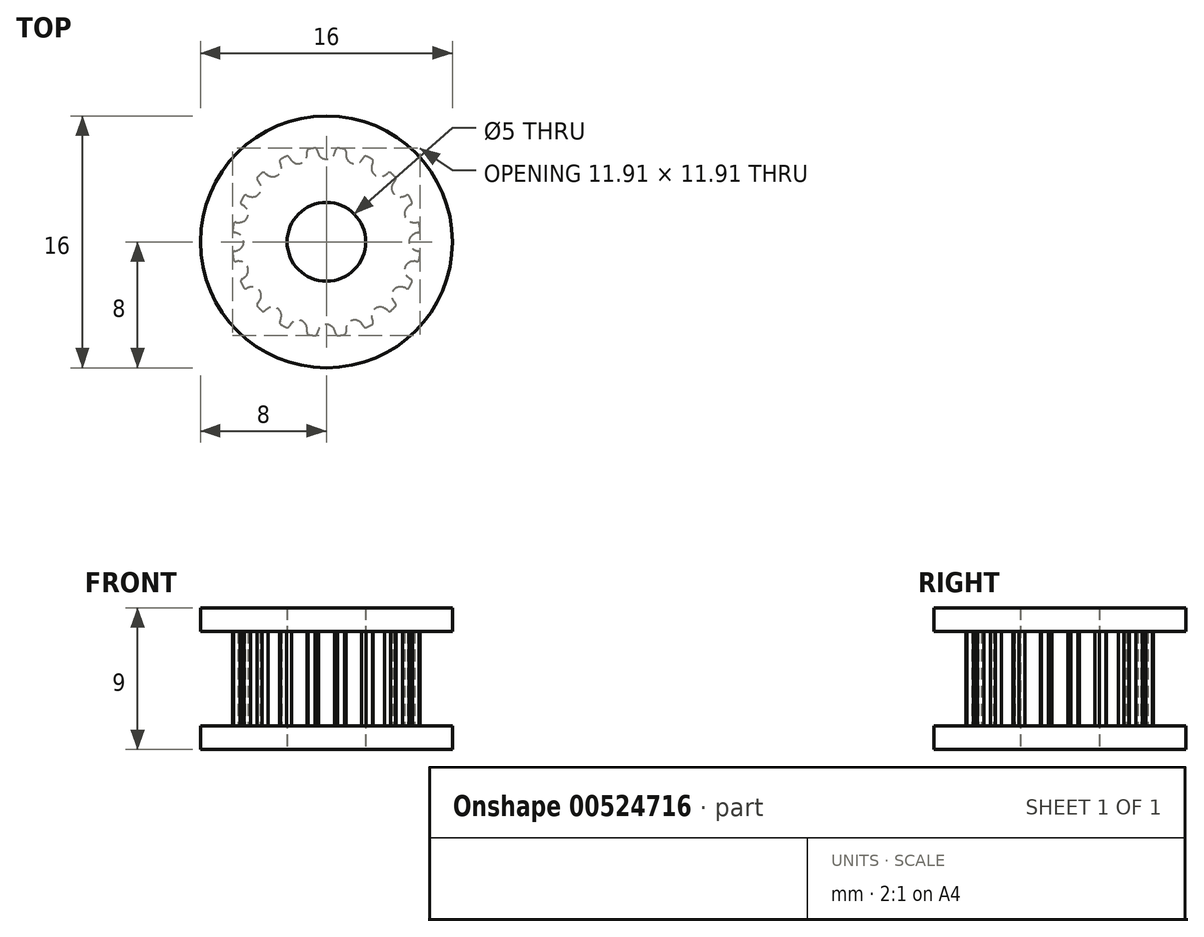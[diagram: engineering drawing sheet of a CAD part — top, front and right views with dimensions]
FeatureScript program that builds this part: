
annotation { "Feature Type Name" : "Feature", "Feature Type Description" : "" }
export const myFeature = defineFeature(function(context is Context, id is Id, definition is map)
    precondition{}
    {
        {
            var Q0;
            Q0=qCreatedBy(makeId("Top.planeOp"),FACE);
            var sketch = newSketch(context, id + "F0", { "sketchPlane" : qUnion([Q0])});
            skLineSegment(sketch, "E0", {"start": v(-19.17, 17.78) * mm, "end": v(-18.17, 17.78) * mm});
            skLineSegment(sketch, "E1", {"start": v(-18.17, 17.78) * mm, "end": v(-18.17, 18.4) * mm});
            skArc(sketch, "E2", {"start": v(-18.67, 18.85) * mm, "mid": v(-18.88, 19.07) * mm, "end": v(-19.17, 19.16) * mm});
            skArc(sketch, "E3", {"start": v(-18.58, 18.54) * mm, "mid": v(-18.61, 18.7) * mm, "end": v(-18.67, 18.85) * mm});
            skArc(sketch, "E4", {"start": v(-18.58, 18.54) * mm, "mid": v(-18.53, 18.44) * mm, "end": v(-18.43, 18.4) * mm});
            skLineSegment(sketch, "E5", {"start": v(-18.43, 18.4) * mm, "end": v(-18.17, 18.4) * mm});
            skArc(sketch, "E6.0.MirrorCS", {"start": v(-19.67, 18.85) * mm, "mid": v(-19.47, 19.07) * mm, "end": v(-19.17, 19.16) * mm});
            skArc(sketch, "E7.0.MirrorCS", {"start": v(-19.76, 18.54) * mm, "mid": v(-19.73, 18.7) * mm, "end": v(-19.67, 18.85) * mm});
            skArc(sketch, "E8.0.MirrorCS", {"start": v(-19.76, 18.54) * mm, "mid": v(-19.81, 18.44) * mm, "end": v(-19.91, 18.4) * mm});
            skLineSegment(sketch, "E9.0.MirrorCS", {"start": v(-19.91, 18.4) * mm, "end": v(-20.17, 18.4) * mm});
            skLineSegment(sketch, "E10.0.MirrorCS", {"start": v(-20.17, 17.78) * mm, "end": v(-20.17, 18.4) * mm});
            skLineSegment(sketch, "E11.0.MirrorCS", {"start": v(-19.17, 17.78) * mm, "end": v(-20.17, 17.78) * mm});
            skLineSegment(sketch, "E12.direction1", {"start": v(-20.17, 17.78) * mm, "end": v(-18.17, 17.78) * mm, "construction": true});
            skLineSegment(sketch, "E13", {"start": v(-20.17, 18.15) * mm, "end": v(-18.17, 18.15) * mm, "construction": true});
            skPoint(sketch, "E14", {"position": v(0, -5.25) * mm});
            skArc(sketch, "E15", {"start": v(0.51, -5.6) * mm, "mid": v(0, -5.25) * mm, "end": v(-0.51, -5.6) * mm});
            skArc(sketch, "E16", {"start": v(-0.51, -5.6) * mm, "mid": v(-0.56, -5.71) * mm, "end": v(-0.59, -5.83) * mm});
            skArc(sketch, "E17", {"start": v(0.59, -5.83) * mm, "mid": v(0.56, -5.71) * mm, "end": v(0.51, -5.6) * mm});
            skArc(sketch, "E18", {"start": v(0.72, -5.96) * mm, "mid": v(0.94, -5.93) * mm, "end": v(1.16, -5.89) * mm});
            skArc(sketch, "E19", {"start": v(0.59, -5.83) * mm, "mid": v(0.66, -5.94) * mm, "end": v(0.8, -5.95) * mm});
            skArc(sketch, "E20", {"start": v(-0.59, -5.83) * mm, "mid": v(-0.66, -5.94) * mm, "end": v(-0.8, -5.95) * mm});
            skArc(sketch, "E21.1.0", {"start": v(2.22, -5.16) * mm, "mid": v(1.62, -5) * mm, "end": v(1.24, -5.48) * mm});
            skPoint(sketch, "E21.1.1", {"position": v(1.62, -5) * mm});
            skArc(sketch, "E21.1.2", {"start": v(1.24, -5.48) * mm, "mid": v(1.23, -5.6) * mm, "end": v(1.24, -5.73) * mm});
            skArc(sketch, "E21.1.3", {"start": v(2.36, -5.37) * mm, "mid": v(2.47, -5.44) * mm, "end": v(2.6, -5.41) * mm});
            skArc(sketch, "E21.1.4", {"start": v(1.24, -5.73) * mm, "mid": v(1.2, -5.85) * mm, "end": v(1.08, -5.9) * mm});
            skArc(sketch, "E21.1.5", {"start": v(2.36, -5.37) * mm, "mid": v(2.3, -5.26) * mm, "end": v(2.22, -5.16) * mm});
            skArc(sketch, "E22.3.2.0", {"start": v(3.7, -4.22) * mm, "mid": v(3.09, -4.25) * mm, "end": v(2.87, -4.83) * mm});
            skPoint(sketch, "E22.4.2.0", {"position": v(3.09, -4.25) * mm});
            skArc(sketch, "E22.5.2.0", {"start": v(2.87, -4.83) * mm, "mid": v(2.9, -4.95) * mm, "end": v(2.95, -5.07) * mm});
            skArc(sketch, "E22.9.2.0", {"start": v(3.9, -4.37) * mm, "mid": v(4.03, -4.41) * mm, "end": v(4.14, -4.35) * mm});
            skArc(sketch, "E22.13.2.0", {"start": v(2.95, -5.07) * mm, "mid": v(2.95, -5.2) * mm, "end": v(2.85, -5.28) * mm});
            skArc(sketch, "E22.17.2.0", {"start": v(3.9, -4.37) * mm, "mid": v(3.81, -4.3) * mm, "end": v(3.7, -4.22) * mm});
            skArc(sketch, "E22.3.3.0", {"start": v(4.83, -2.87) * mm, "mid": v(4.25, -3.09) * mm, "end": v(4.22, -3.7) * mm});
            skPoint(sketch, "E22.4.3.0", {"position": v(4.25, -3.09) * mm});
            skArc(sketch, "E22.5.3.0", {"start": v(4.22, -3.7) * mm, "mid": v(4.3, -3.81) * mm, "end": v(4.37, -3.9) * mm});
            skArc(sketch, "E22.9.3.0", {"start": v(5.07, -2.95) * mm, "mid": v(5.2, -2.95) * mm, "end": v(5.28, -2.85) * mm});
            skArc(sketch, "E22.13.3.0", {"start": v(4.37, -3.9) * mm, "mid": v(4.41, -4.03) * mm, "end": v(4.35, -4.14) * mm});
            skArc(sketch, "E22.17.3.0", {"start": v(5.07, -2.95) * mm, "mid": v(4.95, -2.9) * mm, "end": v(4.83, -2.87) * mm});
            skArc(sketch, "E22.3.4.0", {"start": v(5.48, -1.24) * mm, "mid": v(5, -1.62) * mm, "end": v(5.16, -2.22) * mm});
            skPoint(sketch, "E22.4.4.0", {"position": v(5, -1.62) * mm});
            skArc(sketch, "E22.5.4.0", {"start": v(5.16, -2.22) * mm, "mid": v(5.26, -2.3) * mm, "end": v(5.37, -2.36) * mm});
            skArc(sketch, "E22.9.4.0", {"start": v(5.73, -1.24) * mm, "mid": v(5.85, -1.2) * mm, "end": v(5.9, -1.08) * mm});
            skArc(sketch, "E22.13.4.0", {"start": v(5.37, -2.36) * mm, "mid": v(5.44, -2.47) * mm, "end": v(5.41, -2.6) * mm});
            skArc(sketch, "E22.17.4.0", {"start": v(5.73, -1.24) * mm, "mid": v(5.6, -1.23) * mm, "end": v(5.48, -1.24) * mm});
            skArc(sketch, "E22.3.5.0", {"start": v(5.6, 0.51) * mm, "mid": v(5.25, 0) * mm, "end": v(5.6, -0.51) * mm});
            skPoint(sketch, "E22.4.5.0", {"position": v(5.25, 0) * mm});
            skArc(sketch, "E22.5.5.0", {"start": v(5.6, -0.51) * mm, "mid": v(5.71, -0.56) * mm, "end": v(5.83, -0.59) * mm});
            skArc(sketch, "E22.9.5.0", {"start": v(5.83, 0.59) * mm, "mid": v(5.94, 0.66) * mm, "end": v(5.95, 0.8) * mm});
            skArc(sketch, "E22.13.5.0", {"start": v(5.83, -0.59) * mm, "mid": v(5.94, -0.66) * mm, "end": v(5.95, -0.8) * mm});
            skArc(sketch, "E22.17.5.0", {"start": v(5.83, 0.59) * mm, "mid": v(5.71, 0.56) * mm, "end": v(5.6, 0.51) * mm});
            skArc(sketch, "E22.3.6.0", {"start": v(5.16, 2.22) * mm, "mid": v(5, 1.62) * mm, "end": v(5.48, 1.24) * mm});
            skPoint(sketch, "E22.4.6.0", {"position": v(5, 1.62) * mm});
            skArc(sketch, "E22.5.6.0", {"start": v(5.48, 1.24) * mm, "mid": v(5.6, 1.23) * mm, "end": v(5.73, 1.24) * mm});
            skArc(sketch, "E22.9.6.0", {"start": v(5.37, 2.36) * mm, "mid": v(5.44, 2.47) * mm, "end": v(5.41, 2.6) * mm});
            skArc(sketch, "E22.13.6.0", {"start": v(5.73, 1.24) * mm, "mid": v(5.85, 1.2) * mm, "end": v(5.9, 1.08) * mm});
            skArc(sketch, "E22.17.6.0", {"start": v(5.37, 2.36) * mm, "mid": v(5.26, 2.3) * mm, "end": v(5.16, 2.22) * mm});
            skArc(sketch, "E22.3.7.0", {"start": v(4.22, 3.7) * mm, "mid": v(4.25, 3.09) * mm, "end": v(4.83, 2.87) * mm});
            skPoint(sketch, "E22.4.7.0", {"position": v(4.25, 3.09) * mm});
            skArc(sketch, "E22.5.7.0", {"start": v(4.83, 2.87) * mm, "mid": v(4.95, 2.9) * mm, "end": v(5.07, 2.95) * mm});
            skArc(sketch, "E22.9.7.0", {"start": v(4.37, 3.9) * mm, "mid": v(4.41, 4.03) * mm, "end": v(4.35, 4.14) * mm});
            skArc(sketch, "E22.13.7.0", {"start": v(5.07, 2.95) * mm, "mid": v(5.2, 2.95) * mm, "end": v(5.28, 2.85) * mm});
            skArc(sketch, "E22.17.7.0", {"start": v(4.37, 3.9) * mm, "mid": v(4.3, 3.81) * mm, "end": v(4.22, 3.7) * mm});
            skArc(sketch, "E22.3.8.0", {"start": v(2.87, 4.83) * mm, "mid": v(3.09, 4.25) * mm, "end": v(3.7, 4.22) * mm});
            skPoint(sketch, "E22.4.8.0", {"position": v(3.09, 4.25) * mm});
            skArc(sketch, "E22.5.8.0", {"start": v(3.7, 4.22) * mm, "mid": v(3.81, 4.3) * mm, "end": v(3.9, 4.37) * mm});
            skArc(sketch, "E22.9.8.0", {"start": v(2.95, 5.07) * mm, "mid": v(2.95, 5.2) * mm, "end": v(2.85, 5.28) * mm});
            skArc(sketch, "E22.13.8.0", {"start": v(3.9, 4.37) * mm, "mid": v(4.03, 4.41) * mm, "end": v(4.14, 4.35) * mm});
            skArc(sketch, "E22.17.8.0", {"start": v(2.95, 5.07) * mm, "mid": v(2.9, 4.95) * mm, "end": v(2.87, 4.83) * mm});
            skArc(sketch, "E22.3.9.0", {"start": v(1.24, 5.48) * mm, "mid": v(1.62, 5) * mm, "end": v(2.22, 5.16) * mm});
            skPoint(sketch, "E22.4.9.0", {"position": v(1.62, 5) * mm});
            skArc(sketch, "E22.5.9.0", {"start": v(2.22, 5.16) * mm, "mid": v(2.3, 5.26) * mm, "end": v(2.36, 5.37) * mm});
            skArc(sketch, "E22.9.9.0", {"start": v(1.24, 5.73) * mm, "mid": v(1.2, 5.85) * mm, "end": v(1.08, 5.9) * mm});
            skArc(sketch, "E22.13.9.0", {"start": v(2.36, 5.37) * mm, "mid": v(2.47, 5.44) * mm, "end": v(2.6, 5.41) * mm});
            skArc(sketch, "E22.17.9.0", {"start": v(1.24, 5.73) * mm, "mid": v(1.23, 5.6) * mm, "end": v(1.24, 5.48) * mm});
            skArc(sketch, "E22.3.10.0", {"start": v(-0.51, 5.6) * mm, "mid": v(0, 5.25) * mm, "end": v(0.51, 5.6) * mm});
            skPoint(sketch, "E22.4.10.0", {"position": v(0, 5.25) * mm});
            skArc(sketch, "E22.5.10.0", {"start": v(0.51, 5.6) * mm, "mid": v(0.56, 5.71) * mm, "end": v(0.59, 5.83) * mm});
            skArc(sketch, "E22.9.10.0", {"start": v(-0.59, 5.83) * mm, "mid": v(-0.66, 5.94) * mm, "end": v(-0.8, 5.95) * mm});
            skArc(sketch, "E22.13.10.0", {"start": v(0.59, 5.83) * mm, "mid": v(0.66, 5.94) * mm, "end": v(0.8, 5.95) * mm});
            skArc(sketch, "E22.17.10.0", {"start": v(-0.59, 5.83) * mm, "mid": v(-0.56, 5.71) * mm, "end": v(-0.51, 5.6) * mm});
            skArc(sketch, "E22.3.11.0", {"start": v(-2.22, 5.16) * mm, "mid": v(-1.62, 5) * mm, "end": v(-1.24, 5.48) * mm});
            skPoint(sketch, "E22.4.11.0", {"position": v(-1.62, 5) * mm});
            skArc(sketch, "E22.5.11.0", {"start": v(-1.24, 5.48) * mm, "mid": v(-1.23, 5.6) * mm, "end": v(-1.24, 5.73) * mm});
            skArc(sketch, "E22.9.11.0", {"start": v(-2.36, 5.37) * mm, "mid": v(-2.47, 5.44) * mm, "end": v(-2.6, 5.41) * mm});
            skArc(sketch, "E22.13.11.0", {"start": v(-1.24, 5.73) * mm, "mid": v(-1.2, 5.85) * mm, "end": v(-1.08, 5.9) * mm});
            skArc(sketch, "E22.17.11.0", {"start": v(-2.36, 5.37) * mm, "mid": v(-2.3, 5.26) * mm, "end": v(-2.22, 5.16) * mm});
            skArc(sketch, "E22.3.12.0", {"start": v(-3.7, 4.22) * mm, "mid": v(-3.09, 4.25) * mm, "end": v(-2.87, 4.83) * mm});
            skPoint(sketch, "E22.4.12.0", {"position": v(-3.09, 4.25) * mm});
            skArc(sketch, "E22.5.12.0", {"start": v(-2.87, 4.83) * mm, "mid": v(-2.9, 4.95) * mm, "end": v(-2.95, 5.07) * mm});
            skArc(sketch, "E22.9.12.0", {"start": v(-3.9, 4.37) * mm, "mid": v(-4.03, 4.41) * mm, "end": v(-4.14, 4.35) * mm});
            skArc(sketch, "E22.13.12.0", {"start": v(-2.95, 5.07) * mm, "mid": v(-2.95, 5.2) * mm, "end": v(-2.85, 5.28) * mm});
            skArc(sketch, "E22.17.12.0", {"start": v(-3.9, 4.37) * mm, "mid": v(-3.81, 4.3) * mm, "end": v(-3.7, 4.22) * mm});
            skArc(sketch, "E22.3.13.0", {"start": v(-4.83, 2.87) * mm, "mid": v(-4.25, 3.09) * mm, "end": v(-4.22, 3.7) * mm});
            skPoint(sketch, "E22.4.13.0", {"position": v(-4.25, 3.09) * mm});
            skArc(sketch, "E22.5.13.0", {"start": v(-4.22, 3.7) * mm, "mid": v(-4.3, 3.81) * mm, "end": v(-4.37, 3.9) * mm});
            skArc(sketch, "E22.9.13.0", {"start": v(-5.07, 2.95) * mm, "mid": v(-5.2, 2.95) * mm, "end": v(-5.28, 2.85) * mm});
            skArc(sketch, "E22.13.13.0", {"start": v(-4.37, 3.9) * mm, "mid": v(-4.41, 4.03) * mm, "end": v(-4.35, 4.14) * mm});
            skArc(sketch, "E22.17.13.0", {"start": v(-5.07, 2.95) * mm, "mid": v(-4.95, 2.9) * mm, "end": v(-4.83, 2.87) * mm});
            skArc(sketch, "E22.3.14.0", {"start": v(-5.48, 1.24) * mm, "mid": v(-5, 1.62) * mm, "end": v(-5.16, 2.22) * mm});
            skPoint(sketch, "E22.4.14.0", {"position": v(-5, 1.62) * mm});
            skArc(sketch, "E22.5.14.0", {"start": v(-5.16, 2.22) * mm, "mid": v(-5.26, 2.3) * mm, "end": v(-5.37, 2.36) * mm});
            skArc(sketch, "E22.9.14.0", {"start": v(-5.73, 1.24) * mm, "mid": v(-5.85, 1.2) * mm, "end": v(-5.9, 1.08) * mm});
            skArc(sketch, "E22.13.14.0", {"start": v(-5.37, 2.36) * mm, "mid": v(-5.44, 2.47) * mm, "end": v(-5.41, 2.6) * mm});
            skArc(sketch, "E22.17.14.0", {"start": v(-5.73, 1.24) * mm, "mid": v(-5.6, 1.23) * mm, "end": v(-5.48, 1.24) * mm});
            skArc(sketch, "E22.3.15.0", {"start": v(-5.6, -0.51) * mm, "mid": v(-5.25, 0) * mm, "end": v(-5.6, 0.51) * mm});
            skPoint(sketch, "E22.4.15.0", {"position": v(-5.25, 0) * mm});
            skArc(sketch, "E22.5.15.0", {"start": v(-5.6, 0.51) * mm, "mid": v(-5.71, 0.56) * mm, "end": v(-5.83, 0.59) * mm});
            skArc(sketch, "E22.9.15.0", {"start": v(-5.83, -0.59) * mm, "mid": v(-5.94, -0.66) * mm, "end": v(-5.95, -0.8) * mm});
            skArc(sketch, "E22.13.15.0", {"start": v(-5.83, 0.59) * mm, "mid": v(-5.94, 0.66) * mm, "end": v(-5.95, 0.8) * mm});
            skArc(sketch, "E22.17.15.0", {"start": v(-5.83, -0.59) * mm, "mid": v(-5.71, -0.56) * mm, "end": v(-5.6, -0.51) * mm});
            skArc(sketch, "E22.3.16.0", {"start": v(-5.16, -2.22) * mm, "mid": v(-5, -1.62) * mm, "end": v(-5.48, -1.24) * mm});
            skPoint(sketch, "E22.4.16.0", {"position": v(-5, -1.62) * mm});
            skArc(sketch, "E22.5.16.0", {"start": v(-5.48, -1.24) * mm, "mid": v(-5.6, -1.23) * mm, "end": v(-5.73, -1.24) * mm});
            skArc(sketch, "E22.9.16.0", {"start": v(-5.37, -2.36) * mm, "mid": v(-5.44, -2.47) * mm, "end": v(-5.41, -2.6) * mm});
            skArc(sketch, "E22.13.16.0", {"start": v(-5.73, -1.24) * mm, "mid": v(-5.85, -1.2) * mm, "end": v(-5.9, -1.08) * mm});
            skArc(sketch, "E22.17.16.0", {"start": v(-5.37, -2.36) * mm, "mid": v(-5.26, -2.3) * mm, "end": v(-5.16, -2.22) * mm});
            skArc(sketch, "E22.3.17.0", {"start": v(-4.22, -3.7) * mm, "mid": v(-4.25, -3.09) * mm, "end": v(-4.83, -2.87) * mm});
            skPoint(sketch, "E22.4.17.0", {"position": v(-4.25, -3.09) * mm});
            skArc(sketch, "E22.5.17.0", {"start": v(-4.83, -2.87) * mm, "mid": v(-4.95, -2.9) * mm, "end": v(-5.07, -2.95) * mm});
            skArc(sketch, "E22.9.17.0", {"start": v(-4.37, -3.9) * mm, "mid": v(-4.41, -4.03) * mm, "end": v(-4.35, -4.14) * mm});
            skArc(sketch, "E22.13.17.0", {"start": v(-5.07, -2.95) * mm, "mid": v(-5.2, -2.95) * mm, "end": v(-5.28, -2.85) * mm});
            skArc(sketch, "E22.17.17.0", {"start": v(-4.37, -3.9) * mm, "mid": v(-4.3, -3.81) * mm, "end": v(-4.22, -3.7) * mm});
            skArc(sketch, "E22.3.18.0", {"start": v(-2.87, -4.83) * mm, "mid": v(-3.09, -4.25) * mm, "end": v(-3.7, -4.22) * mm});
            skPoint(sketch, "E22.4.18.0", {"position": v(-3.09, -4.25) * mm});
            skArc(sketch, "E22.5.18.0", {"start": v(-3.7, -4.22) * mm, "mid": v(-3.81, -4.3) * mm, "end": v(-3.9, -4.37) * mm});
            skArc(sketch, "E22.9.18.0", {"start": v(-2.95, -5.07) * mm, "mid": v(-2.95, -5.2) * mm, "end": v(-2.85, -5.28) * mm});
            skArc(sketch, "E22.13.18.0", {"start": v(-3.9, -4.37) * mm, "mid": v(-4.03, -4.41) * mm, "end": v(-4.14, -4.35) * mm});
            skArc(sketch, "E22.17.18.0", {"start": v(-2.95, -5.07) * mm, "mid": v(-2.9, -4.95) * mm, "end": v(-2.87, -4.83) * mm});
            skArc(sketch, "E22.3.19.0", {"start": v(-1.24, -5.48) * mm, "mid": v(-1.62, -5) * mm, "end": v(-2.22, -5.16) * mm});
            skPoint(sketch, "E22.4.19.0", {"position": v(-1.62, -5) * mm});
            skArc(sketch, "E22.5.19.0", {"start": v(-2.22, -5.16) * mm, "mid": v(-2.3, -5.26) * mm, "end": v(-2.36, -5.37) * mm});
            skArc(sketch, "E22.9.19.0", {"start": v(-1.24, -5.73) * mm, "mid": v(-1.2, -5.85) * mm, "end": v(-1.08, -5.9) * mm});
            skArc(sketch, "E22.13.19.0", {"start": v(-2.36, -5.37) * mm, "mid": v(-2.47, -5.44) * mm, "end": v(-2.6, -5.41) * mm});
            skArc(sketch, "E22.17.19.0", {"start": v(-1.24, -5.73) * mm, "mid": v(-1.23, -5.6) * mm, "end": v(-1.24, -5.48) * mm});
            skArc(sketch, "E23.trimOffspring", {"start": v(2.52, -5.44) * mm, "mid": v(2.72, -5.35) * mm, "end": v(2.92, -5.24) * mm});
            skArc(sketch, "E24.trimOffspring", {"start": v(4.08, -4.4) * mm, "mid": v(4.24, -4.24) * mm, "end": v(4.4, -4.08) * mm});
            skArc(sketch, "E25.trimOffspring", {"start": v(5.24, -2.92) * mm, "mid": v(5.33, -2.76) * mm, "end": v(5.41, -2.6) * mm});
            skArc(sketch, "E26.trimOffspring", {"start": v(5.89, -1.16) * mm, "mid": v(5.93, -0.94) * mm, "end": v(5.96, -0.72) * mm});
            skArc(sketch, "E27.trimOffspring", {"start": v(5.44, 2.52) * mm, "mid": v(5.35, 2.72) * mm, "end": v(5.24, 2.92) * mm});
            skArc(sketch, "E28.trimOffspring", {"start": v(4.4, 4.08) * mm, "mid": v(4.24, 4.24) * mm, "end": v(4.08, 4.4) * mm});
            skArc(sketch, "E29.trimOffspring", {"start": v(5.96, 0.72) * mm, "mid": v(5.93, 0.94) * mm, "end": v(5.89, 1.16) * mm});
            skArc(sketch, "E30.trimOffspring", {"start": v(2.92, 5.24) * mm, "mid": v(2.72, 5.35) * mm, "end": v(2.52, 5.44) * mm});
            skArc(sketch, "E31.trimOffspring", {"start": v(1.16, 5.89) * mm, "mid": v(0.94, 5.93) * mm, "end": v(0.72, 5.96) * mm});
            skArc(sketch, "E32.trimOffspring", {"start": v(-0.72, 5.96) * mm, "mid": v(-0.94, 5.93) * mm, "end": v(-1.16, 5.89) * mm});
            skArc(sketch, "E33.trimOffspring", {"start": v(-2.52, 5.44) * mm, "mid": v(-2.72, 5.35) * mm, "end": v(-2.92, 5.24) * mm});
            skArc(sketch, "E34.trimOffspring", {"start": v(-4.08, 4.4) * mm, "mid": v(-4.24, 4.24) * mm, "end": v(-4.4, 4.08) * mm});
            skArc(sketch, "E35.trimOffspring", {"start": v(-5.24, 2.92) * mm, "mid": v(-5.35, 2.72) * mm, "end": v(-5.44, 2.52) * mm});
            skArc(sketch, "E36.trimOffspring", {"start": v(-5.89, 1.16) * mm, "mid": v(-5.93, 0.94) * mm, "end": v(-5.96, 0.72) * mm});
            skArc(sketch, "E37.trimOffspring", {"start": v(-5.96, -0.72) * mm, "mid": v(-5.93, -0.94) * mm, "end": v(-5.89, -1.16) * mm});
            skArc(sketch, "E38.trimOffspring", {"start": v(-5.44, -2.52) * mm, "mid": v(-5.35, -2.72) * mm, "end": v(-5.24, -2.92) * mm});
            skArc(sketch, "E39.trimOffspring", {"start": v(-4.4, -4.08) * mm, "mid": v(-4.24, -4.24) * mm, "end": v(-4.08, -4.4) * mm});
            skArc(sketch, "E40.trimOffspring", {"start": v(-2.92, -5.24) * mm, "mid": v(-2.72, -5.35) * mm, "end": v(-2.52, -5.44) * mm});
            skArc(sketch, "E41.trimOffspring", {"start": v(-1.16, -5.89) * mm, "mid": v(-0.94, -5.93) * mm, "end": v(-0.72, -5.96) * mm});
            skSolve(sketch);
        }
        {
            var Q0;
            Q0=makeQuery(id+"F0.imprint","IMPRINT",FACE,{"disambiguationData":[TD([[makeQuery(id+"F0.imprint","IMPRINT",EDGE,{"derivedFrom":sQuery(id+"F0.wireOp",EDGE,"E15")}),-1.0]])]});
            extrude(context, id + "F1", {"entities" : qUnion([Q0]), "depth" : 6 * mm, "offsetDistance" : 25 * mm});
        }
        {
            var Q0;
            Q0=makeQuery(id+"F1.opExtrude","CAP_FACE",FACE,{"disambiguationData":[OSD([sQuery(id+"F0.wireOp",EDGE,"E15"),sQuery(id+"F0.wireOp",EDGE,"E16"),sQuery(id+"F0.wireOp",EDGE,"E17"),sQuery(id+"F0.wireOp",EDGE,"E18"),sQuery(id+"F0.wireOp",EDGE,"E19"),sQuery(id+"F0.wireOp",EDGE,"E20"),sQuery(id+"F0.wireOp",EDGE,"E21.1.0"),sQuery(id+"F0.wireOp",EDGE,"E21.1.2"),sQuery(id+"F0.wireOp",EDGE,"E21.1.3"),sQuery(id+"F0.wireOp",EDGE,"E21.1.4"),sQuery(id+"F0.wireOp",EDGE,"E21.1.5"),sQuery(id+"F0.wireOp",EDGE,"E22.3.2.0"),sQuery(id+"F0.wireOp",EDGE,"E22.5.2.0"),sQuery(id+"F0.wireOp",EDGE,"E22.9.2.0"),sQuery(id+"F0.wireOp",EDGE,"E22.13.2.0"),sQuery(id+"F0.wireOp",EDGE,"E22.17.2.0"),sQuery(id+"F0.wireOp",EDGE,"E22.3.3.0"),sQuery(id+"F0.wireOp",EDGE,"E22.5.3.0"),sQuery(id+"F0.wireOp",EDGE,"E22.9.3.0"),sQuery(id+"F0.wireOp",EDGE,"E22.13.3.0"),sQuery(id+"F0.wireOp",EDGE,"E22.17.3.0"),sQuery(id+"F0.wireOp",EDGE,"E22.3.4.0"),sQuery(id+"F0.wireOp",EDGE,"E22.5.4.0"),sQuery(id+"F0.wireOp",EDGE,"E22.9.4.0"),sQuery(id+"F0.wireOp",EDGE,"E22.13.4.0"),sQuery(id+"F0.wireOp",EDGE,"E22.17.4.0"),sQuery(id+"F0.wireOp",EDGE,"E22.3.5.0"),sQuery(id+"F0.wireOp",EDGE,"E22.5.5.0"),sQuery(id+"F0.wireOp",EDGE,"E22.9.5.0"),sQuery(id+"F0.wireOp",EDGE,"E22.13.5.0"),sQuery(id+"F0.wireOp",EDGE,"E22.17.5.0"),sQuery(id+"F0.wireOp",EDGE,"E22.3.6.0"),sQuery(id+"F0.wireOp",EDGE,"E22.5.6.0"),sQuery(id+"F0.wireOp",EDGE,"E22.9.6.0"),sQuery(id+"F0.wireOp",EDGE,"E22.13.6.0"),sQuery(id+"F0.wireOp",EDGE,"E22.17.6.0"),sQuery(id+"F0.wireOp",EDGE,"E22.3.7.0"),sQuery(id+"F0.wireOp",EDGE,"E22.5.7.0"),sQuery(id+"F0.wireOp",EDGE,"E22.9.7.0"),sQuery(id+"F0.wireOp",EDGE,"E22.13.7.0"),sQuery(id+"F0.wireOp",EDGE,"E22.17.7.0"),sQuery(id+"F0.wireOp",EDGE,"E22.3.8.0"),sQuery(id+"F0.wireOp",EDGE,"E22.5.8.0"),sQuery(id+"F0.wireOp",EDGE,"E22.9.8.0"),sQuery(id+"F0.wireOp",EDGE,"E22.13.8.0"),sQuery(id+"F0.wireOp",EDGE,"E22.17.8.0"),sQuery(id+"F0.wireOp",EDGE,"E22.3.9.0"),sQuery(id+"F0.wireOp",EDGE,"E22.5.9.0"),sQuery(id+"F0.wireOp",EDGE,"E22.9.9.0"),sQuery(id+"F0.wireOp",EDGE,"E22.13.9.0"),sQuery(id+"F0.wireOp",EDGE,"E22.17.9.0"),sQuery(id+"F0.wireOp",EDGE,"E22.3.10.0"),sQuery(id+"F0.wireOp",EDGE,"E22.5.10.0"),sQuery(id+"F0.wireOp",EDGE,"E22.9.10.0"),sQuery(id+"F0.wireOp",EDGE,"E22.13.10.0"),sQuery(id+"F0.wireOp",EDGE,"E22.17.10.0"),sQuery(id+"F0.wireOp",EDGE,"E22.3.11.0"),sQuery(id+"F0.wireOp",EDGE,"E22.5.11.0"),sQuery(id+"F0.wireOp",EDGE,"E22.9.11.0"),sQuery(id+"F0.wireOp",EDGE,"E22.13.11.0"),sQuery(id+"F0.wireOp",EDGE,"E22.17.11.0"),sQuery(id+"F0.wireOp",EDGE,"E22.3.12.0"),sQuery(id+"F0.wireOp",EDGE,"E22.5.12.0"),sQuery(id+"F0.wireOp",EDGE,"E22.9.12.0"),sQuery(id+"F0.wireOp",EDGE,"E22.13.12.0"),sQuery(id+"F0.wireOp",EDGE,"E22.17.12.0"),sQuery(id+"F0.wireOp",EDGE,"E22.3.13.0"),sQuery(id+"F0.wireOp",EDGE,"E22.5.13.0"),sQuery(id+"F0.wireOp",EDGE,"E22.9.13.0"),sQuery(id+"F0.wireOp",EDGE,"E22.13.13.0"),sQuery(id+"F0.wireOp",EDGE,"E22.17.13.0"),sQuery(id+"F0.wireOp",EDGE,"E22.3.14.0"),sQuery(id+"F0.wireOp",EDGE,"E22.5.14.0"),sQuery(id+"F0.wireOp",EDGE,"E22.9.14.0"),sQuery(id+"F0.wireOp",EDGE,"E22.13.14.0"),sQuery(id+"F0.wireOp",EDGE,"E22.17.14.0"),sQuery(id+"F0.wireOp",EDGE,"E22.3.15.0"),sQuery(id+"F0.wireOp",EDGE,"E22.5.15.0"),sQuery(id+"F0.wireOp",EDGE,"E22.9.15.0"),sQuery(id+"F0.wireOp",EDGE,"E22.13.15.0"),sQuery(id+"F0.wireOp",EDGE,"E22.17.15.0"),sQuery(id+"F0.wireOp",EDGE,"E22.3.16.0"),sQuery(id+"F0.wireOp",EDGE,"E22.5.16.0"),sQuery(id+"F0.wireOp",EDGE,"E22.9.16.0"),sQuery(id+"F0.wireOp",EDGE,"E22.13.16.0"),sQuery(id+"F0.wireOp",EDGE,"E22.17.16.0"),sQuery(id+"F0.wireOp",EDGE,"E22.3.17.0"),sQuery(id+"F0.wireOp",EDGE,"E22.5.17.0"),sQuery(id+"F0.wireOp",EDGE,"E22.9.17.0"),sQuery(id+"F0.wireOp",EDGE,"E22.13.17.0"),sQuery(id+"F0.wireOp",EDGE,"E22.17.17.0"),sQuery(id+"F0.wireOp",EDGE,"E22.3.18.0"),sQuery(id+"F0.wireOp",EDGE,"E22.5.18.0"),sQuery(id+"F0.wireOp",EDGE,"E22.9.18.0"),sQuery(id+"F0.wireOp",EDGE,"E22.13.18.0"),sQuery(id+"F0.wireOp",EDGE,"E22.17.18.0"),sQuery(id+"F0.wireOp",EDGE,"E22.3.19.0"),sQuery(id+"F0.wireOp",EDGE,"E22.5.19.0"),sQuery(id+"F0.wireOp",EDGE,"E22.9.19.0"),sQuery(id+"F0.wireOp",EDGE,"E22.13.19.0"),sQuery(id+"F0.wireOp",EDGE,"E22.17.19.0"),sQuery(id+"F0.wireOp",EDGE,"E23.trimOffspring"),sQuery(id+"F0.wireOp",EDGE,"E24.trimOffspring"),sQuery(id+"F0.wireOp",EDGE,"E25.trimOffspring"),sQuery(id+"F0.wireOp",EDGE,"E26.trimOffspring"),sQuery(id+"F0.wireOp",EDGE,"E27.trimOffspring"),sQuery(id+"F0.wireOp",EDGE,"E28.trimOffspring"),sQuery(id+"F0.wireOp",EDGE,"E29.trimOffspring"),sQuery(id+"F0.wireOp",EDGE,"E30.trimOffspring"),sQuery(id+"F0.wireOp",EDGE,"E31.trimOffspring"),sQuery(id+"F0.wireOp",EDGE,"E32.trimOffspring"),sQuery(id+"F0.wireOp",EDGE,"E33.trimOffspring"),sQuery(id+"F0.wireOp",EDGE,"E34.trimOffspring"),sQuery(id+"F0.wireOp",EDGE,"E35.trimOffspring"),sQuery(id+"F0.wireOp",EDGE,"E36.trimOffspring"),sQuery(id+"F0.wireOp",EDGE,"E37.trimOffspring"),sQuery(id+"F0.wireOp",EDGE,"E38.trimOffspring"),sQuery(id+"F0.wireOp",EDGE,"E39.trimOffspring"),sQuery(id+"F0.wireOp",EDGE,"E40.trimOffspring"),sQuery(id+"F0.wireOp",EDGE,"E41.trimOffspring")])],"isStart":false});
            var sketch = newSketch(context, id + "F2", { "sketchPlane" : qUnion([Q0])});
            skCircle(sketch, "E42", {"center": v(0, 0) * mm, "radius": 8 * mm});
            skSolve(sketch);
        }
        {
            var Q0;
            Q0=qSketchRegion(id+"F2",true);
            extrude(context, id + "F3", {"entities" : qUnion([Q0]), "operationType" : NewBodyOperationType.ADD, "depth" : 1.5 * mm, "offsetDistance" : 25 * mm});
        }
        {
            var Q0;
            Q0=makeQuery(id+"F1.opExtrude","CAP_FACE",FACE,{"disambiguationData":[OSD([sQuery(id+"F0.wireOp",EDGE,"E15"),sQuery(id+"F0.wireOp",EDGE,"E16"),sQuery(id+"F0.wireOp",EDGE,"E17"),sQuery(id+"F0.wireOp",EDGE,"E18"),sQuery(id+"F0.wireOp",EDGE,"E19"),sQuery(id+"F0.wireOp",EDGE,"E20"),sQuery(id+"F0.wireOp",EDGE,"E21.1.0"),sQuery(id+"F0.wireOp",EDGE,"E21.1.2"),sQuery(id+"F0.wireOp",EDGE,"E21.1.3"),sQuery(id+"F0.wireOp",EDGE,"E21.1.4"),sQuery(id+"F0.wireOp",EDGE,"E21.1.5"),sQuery(id+"F0.wireOp",EDGE,"E22.3.2.0"),sQuery(id+"F0.wireOp",EDGE,"E22.5.2.0"),sQuery(id+"F0.wireOp",EDGE,"E22.9.2.0"),sQuery(id+"F0.wireOp",EDGE,"E22.13.2.0"),sQuery(id+"F0.wireOp",EDGE,"E22.17.2.0"),sQuery(id+"F0.wireOp",EDGE,"E22.3.3.0"),sQuery(id+"F0.wireOp",EDGE,"E22.5.3.0"),sQuery(id+"F0.wireOp",EDGE,"E22.9.3.0"),sQuery(id+"F0.wireOp",EDGE,"E22.13.3.0"),sQuery(id+"F0.wireOp",EDGE,"E22.17.3.0"),sQuery(id+"F0.wireOp",EDGE,"E22.3.4.0"),sQuery(id+"F0.wireOp",EDGE,"E22.5.4.0"),sQuery(id+"F0.wireOp",EDGE,"E22.9.4.0"),sQuery(id+"F0.wireOp",EDGE,"E22.13.4.0"),sQuery(id+"F0.wireOp",EDGE,"E22.17.4.0"),sQuery(id+"F0.wireOp",EDGE,"E22.3.5.0"),sQuery(id+"F0.wireOp",EDGE,"E22.5.5.0"),sQuery(id+"F0.wireOp",EDGE,"E22.9.5.0"),sQuery(id+"F0.wireOp",EDGE,"E22.13.5.0"),sQuery(id+"F0.wireOp",EDGE,"E22.17.5.0"),sQuery(id+"F0.wireOp",EDGE,"E22.3.6.0"),sQuery(id+"F0.wireOp",EDGE,"E22.5.6.0"),sQuery(id+"F0.wireOp",EDGE,"E22.9.6.0"),sQuery(id+"F0.wireOp",EDGE,"E22.13.6.0"),sQuery(id+"F0.wireOp",EDGE,"E22.17.6.0"),sQuery(id+"F0.wireOp",EDGE,"E22.3.7.0"),sQuery(id+"F0.wireOp",EDGE,"E22.5.7.0"),sQuery(id+"F0.wireOp",EDGE,"E22.9.7.0"),sQuery(id+"F0.wireOp",EDGE,"E22.13.7.0"),sQuery(id+"F0.wireOp",EDGE,"E22.17.7.0"),sQuery(id+"F0.wireOp",EDGE,"E22.3.8.0"),sQuery(id+"F0.wireOp",EDGE,"E22.5.8.0"),sQuery(id+"F0.wireOp",EDGE,"E22.9.8.0"),sQuery(id+"F0.wireOp",EDGE,"E22.13.8.0"),sQuery(id+"F0.wireOp",EDGE,"E22.17.8.0"),sQuery(id+"F0.wireOp",EDGE,"E22.3.9.0"),sQuery(id+"F0.wireOp",EDGE,"E22.5.9.0"),sQuery(id+"F0.wireOp",EDGE,"E22.9.9.0"),sQuery(id+"F0.wireOp",EDGE,"E22.13.9.0"),sQuery(id+"F0.wireOp",EDGE,"E22.17.9.0"),sQuery(id+"F0.wireOp",EDGE,"E22.3.10.0"),sQuery(id+"F0.wireOp",EDGE,"E22.5.10.0"),sQuery(id+"F0.wireOp",EDGE,"E22.9.10.0"),sQuery(id+"F0.wireOp",EDGE,"E22.13.10.0"),sQuery(id+"F0.wireOp",EDGE,"E22.17.10.0"),sQuery(id+"F0.wireOp",EDGE,"E22.3.11.0"),sQuery(id+"F0.wireOp",EDGE,"E22.5.11.0"),sQuery(id+"F0.wireOp",EDGE,"E22.9.11.0"),sQuery(id+"F0.wireOp",EDGE,"E22.13.11.0"),sQuery(id+"F0.wireOp",EDGE,"E22.17.11.0"),sQuery(id+"F0.wireOp",EDGE,"E22.3.12.0"),sQuery(id+"F0.wireOp",EDGE,"E22.5.12.0"),sQuery(id+"F0.wireOp",EDGE,"E22.9.12.0"),sQuery(id+"F0.wireOp",EDGE,"E22.13.12.0"),sQuery(id+"F0.wireOp",EDGE,"E22.17.12.0"),sQuery(id+"F0.wireOp",EDGE,"E22.3.13.0"),sQuery(id+"F0.wireOp",EDGE,"E22.5.13.0"),sQuery(id+"F0.wireOp",EDGE,"E22.9.13.0"),sQuery(id+"F0.wireOp",EDGE,"E22.13.13.0"),sQuery(id+"F0.wireOp",EDGE,"E22.17.13.0"),sQuery(id+"F0.wireOp",EDGE,"E22.3.14.0"),sQuery(id+"F0.wireOp",EDGE,"E22.5.14.0"),sQuery(id+"F0.wireOp",EDGE,"E22.9.14.0"),sQuery(id+"F0.wireOp",EDGE,"E22.13.14.0"),sQuery(id+"F0.wireOp",EDGE,"E22.17.14.0"),sQuery(id+"F0.wireOp",EDGE,"E22.3.15.0"),sQuery(id+"F0.wireOp",EDGE,"E22.5.15.0"),sQuery(id+"F0.wireOp",EDGE,"E22.9.15.0"),sQuery(id+"F0.wireOp",EDGE,"E22.13.15.0"),sQuery(id+"F0.wireOp",EDGE,"E22.17.15.0"),sQuery(id+"F0.wireOp",EDGE,"E22.3.16.0"),sQuery(id+"F0.wireOp",EDGE,"E22.5.16.0"),sQuery(id+"F0.wireOp",EDGE,"E22.9.16.0"),sQuery(id+"F0.wireOp",EDGE,"E22.13.16.0"),sQuery(id+"F0.wireOp",EDGE,"E22.17.16.0"),sQuery(id+"F0.wireOp",EDGE,"E22.3.17.0"),sQuery(id+"F0.wireOp",EDGE,"E22.5.17.0"),sQuery(id+"F0.wireOp",EDGE,"E22.9.17.0"),sQuery(id+"F0.wireOp",EDGE,"E22.13.17.0"),sQuery(id+"F0.wireOp",EDGE,"E22.17.17.0"),sQuery(id+"F0.wireOp",EDGE,"E22.3.18.0"),sQuery(id+"F0.wireOp",EDGE,"E22.5.18.0"),sQuery(id+"F0.wireOp",EDGE,"E22.9.18.0"),sQuery(id+"F0.wireOp",EDGE,"E22.13.18.0"),sQuery(id+"F0.wireOp",EDGE,"E22.17.18.0"),sQuery(id+"F0.wireOp",EDGE,"E22.3.19.0"),sQuery(id+"F0.wireOp",EDGE,"E22.5.19.0"),sQuery(id+"F0.wireOp",EDGE,"E22.9.19.0"),sQuery(id+"F0.wireOp",EDGE,"E22.13.19.0"),sQuery(id+"F0.wireOp",EDGE,"E22.17.19.0"),sQuery(id+"F0.wireOp",EDGE,"E23.trimOffspring"),sQuery(id+"F0.wireOp",EDGE,"E24.trimOffspring"),sQuery(id+"F0.wireOp",EDGE,"E25.trimOffspring"),sQuery(id+"F0.wireOp",EDGE,"E26.trimOffspring"),sQuery(id+"F0.wireOp",EDGE,"E27.trimOffspring"),sQuery(id+"F0.wireOp",EDGE,"E28.trimOffspring"),sQuery(id+"F0.wireOp",EDGE,"E29.trimOffspring"),sQuery(id+"F0.wireOp",EDGE,"E30.trimOffspring"),sQuery(id+"F0.wireOp",EDGE,"E31.trimOffspring"),sQuery(id+"F0.wireOp",EDGE,"E32.trimOffspring"),sQuery(id+"F0.wireOp",EDGE,"E33.trimOffspring"),sQuery(id+"F0.wireOp",EDGE,"E34.trimOffspring"),sQuery(id+"F0.wireOp",EDGE,"E35.trimOffspring"),sQuery(id+"F0.wireOp",EDGE,"E36.trimOffspring"),sQuery(id+"F0.wireOp",EDGE,"E37.trimOffspring"),sQuery(id+"F0.wireOp",EDGE,"E38.trimOffspring"),sQuery(id+"F0.wireOp",EDGE,"E39.trimOffspring"),sQuery(id+"F0.wireOp",EDGE,"E40.trimOffspring"),sQuery(id+"F0.wireOp",EDGE,"E41.trimOffspring")])],"isStart":true});
            var sketch = newSketch(context, id + "F4", { "sketchPlane" : qUnion([Q0])});
            skCircle(sketch, "E43", {"center": v(0, 0) * mm, "radius": 8 * mm});
            skSolve(sketch);
        }
        {
            var Q0;
            Q0=qSketchRegion(id+"F4",true);
            extrude(context, id + "F5", {"entities" : qUnion([Q0]), "operationType" : NewBodyOperationType.ADD, "depth" : 1.5 * mm, "offsetDistance" : 25 * mm});
        }
        {
            var Q0;
            Q0=makeQuery(id+"F5.opExtrude","CAP_FACE",FACE,{"disambiguationData":[OSD([sQuery(id+"F4.wireOp",EDGE,"E43")])],"isStart":false});
            var sketch = newSketch(context, id + "F6", { "sketchPlane" : qUnion([Q0])});
            skCircle(sketch, "E44", {"center": v(0, 0) * mm, "radius": 2.5 * mm});
            skSolve(sketch);
        }
        {
            var Q0;
            Q0=qSketchRegion(id+"F6",true);
            extrude(context, id + "F7", {"entities" : qUnion([Q0]), "operationType" : NewBodyOperationType.REMOVE, "endBound" : BoundingType.THROUGH_ALL, "oppositeDirection" : true, "depth" : 25 * mm, "offsetDistance" : 25 * mm});
        }
    });
